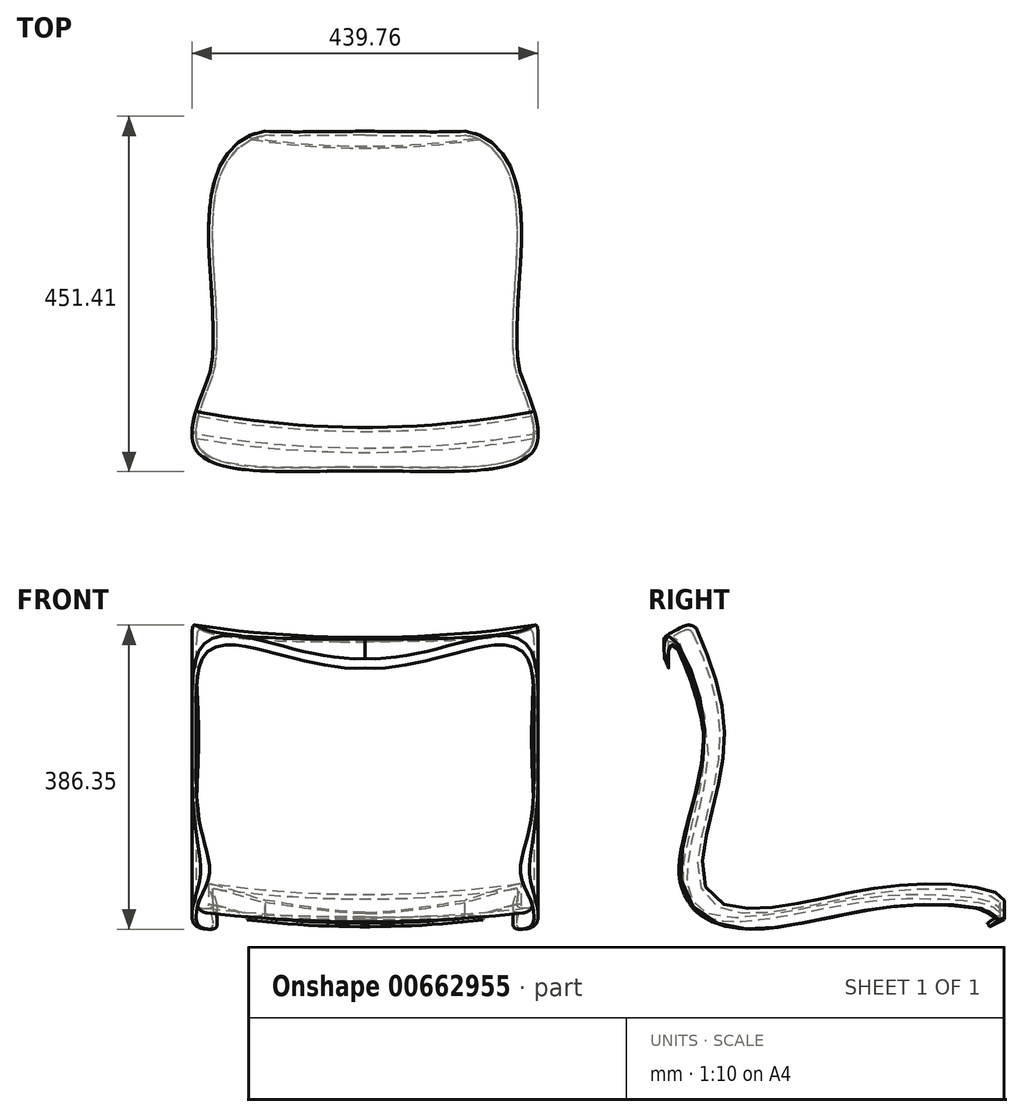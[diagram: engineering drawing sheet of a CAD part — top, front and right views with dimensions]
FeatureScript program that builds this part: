
annotation { "Feature Type Name" : "Feature", "Feature Type Description" : "" }
export const myFeature = defineFeature(function(context is Context, id is Id, definition is map)
    precondition{}
    {
        {
            var Q0;
            Q0=qCreatedBy(makeId("Right.planeOp"),FACE);
            var sketch = newSketch(context, id + "F0", { "sketchPlane" : qUnion([Q0])});
            skFitSpline(sketch, "E0", {"points": [v(-203.66, 209.62) * mm, v(-162.36, 57.64) * mm, v(-188.8, -91.05) * mm, v(-162.36, -145.98) * mm, v(12.76, -129.04) * mm, v(138.3, -122.44) * mm, v(204.4, -134) * mm, v(217.6, -150.52) * mm], "startDerivative": vector(355.5, -818.25) * mm, "endDerivative": vector(135.77, -275.04) * mm});
            skLineSegment(sketch, "E1", {"start": v(473.06, 770.55) * mm, "end": v(854.91, 242.64) * mm, "construction": true});
            skFitSpline(sketch, "E2.0", {"points": [v(-226.96, 199.5) * mm, v(-223.26, 191) * mm, v(-215.95, 174.12) * mm, v(-207.6, 153.32) * mm, v(-201.72, 136.84) * mm, v(-197.79, 124.55) * mm, v(-194.4, 112.35) * mm, v(-191.62, 100.21) * mm, v(-189.51, 88.14) * mm, v(-188.38, 78.11) * mm, v(-187.86, 70.1) * mm, v(-187.72, 65.1) * mm, v(-187.7, 61.1) * mm, v(-187.75, 58.09) * mm, v(-187.85, 55.06) * mm, v(-188.05, 50.99) * mm, v(-188.44, 45.82) * mm, v(-189.33, 37.4) * mm, v(-190.89, 26.65) * mm, v(-193.35, 13.47) * mm, v(-196.24, 0.13) * mm, v(-199.42, -13.31) * mm, v(-202.7, -26.76) * mm, v(-205.94, -40.17) * mm, v(-208.93, -53.5) * mm, v(-211.07, -64.52) * mm, v(-212.47, -73.3) * mm, v(-213.33, -79.87) * mm, v(-213.98, -86.42) * mm, v(-214.36, -92.98) * mm, v(-214.45, -99.5) * mm, v(-214.14, -108.15) * mm, v(-213.1, -116.75) * mm, v(-211.11, -125.26) * mm, v(-209.09, -131.58) * mm, v(-206.46, -137.79) * mm, v(-203.17, -143.82) * mm, v(-199.19, -149.56) * mm, v(-194.5, -154.92) * mm, v(-189.16, -159.75) * mm, v(-184.21, -163.27) * mm, v(-180.02, -165.74) * mm, v(-176.76, -167.43) * mm, v(-173.4, -168.94) * mm, v(-169.96, -170.29) * mm, v(-166.48, -171.44) * mm, v(-161.82, -172.77) * mm, v(-155.94, -174.06) * mm, v(-148.8, -175.11) * mm, v(-139.13, -175.98) * mm, v(-126.76, -176.2) * mm, v(-111.4, -175.4) * mm, v(-95.57, -173.78) * mm, v(-79.36, -171.54) * mm, v(-62.91, -168.84) * mm, v(-46.38, -165.85) * mm, v(-29.96, -162.72) * mm, v(-16.53, -160.13) * mm, v(-6.05, -158.15) * mm, v(1.66, -156.73) * mm, v(7.93, -155.61) * mm, v(12.84, -154.77) * mm, v(16.45, -154.17) * mm, v(20.02, -153.6) * mm, v(24.7, -152.88) * mm, v(30.45, -152.04) * mm, v(37.17, -151.14) * mm, v(45.9, -150.07) * mm, v(56.43, -148.98) * mm, v(68.52, -148) * mm, v(80.14, -147.35) * mm, v(91.37, -146.98) * mm, v(102.29, -146.85) * mm, v(112.98, -146.94) * mm, v(121.76, -147.16) * mm, v(128.75, -147.42) * mm, v(133.12, -147.61) * mm, v(136.6, -147.78) * mm, v(140.1, -147.96) * mm, v(144.41, -148.2) * mm, v(149.5, -148.52) * mm, v(156.12, -149) * mm, v(164.02, -149.73) * mm, v(171.22, -150.64) * mm, v(176.41, -151.48) * mm, v(179.98, -152.16) * mm, v(183.17, -152.88) * mm, v(185.93, -153.63) * mm, v(187.83, -154.25) * mm, v(189.06, -154.7) * mm, v(189.84, -155.03) * mm, v(190.47, -155.31) * mm, v(190.85, -155.5) * mm, v(191.07, -155.63) * mm, v(191.2, -155.7) * mm, v(191.27, -155.75) * mm, v(191.37, -155.81) * mm, v(191.44, -155.87) * mm, v(191.52, -155.93) * mm, v(191.58, -155.98) * mm, v(191.72, -156.13) * mm, v(192, -156.5) * mm, v(192.45, -157.18) * mm, v(193.06, -158.25) * mm, v(193.84, -159.75) * mm, v(194.48, -161.05) * mm, v(194.83, -161.76) * mm]});
            skLineSegment(sketch, "E3", {"start": v(-203.66, 209.62) * mm, "end": v(-226.96, 199.5) * mm});
            skLineSegment(sketch, "E4", {"start": v(194.83, -161.76) * mm, "end": v(217.6, -150.52) * mm});
            skSolve(sketch);
        }
        {
            var Q0;
            Q0 = qSketchRegion(id + "F0", true);
            var Q1;
            Q1 = qConstructionFilter(qBodyType(qCreatedBy(id + "F0" ,EDGE), BodyType.WIRE), ConstructionObject.NO);
            var Q2;
            Q2=sQuery(id+"F0.wireOp",EDGE,"E1");
            revolve(context, id + "F1", {"entities" : qUnion([Q0]), "surfaceEntities" : qUnion([Q1]), "axis" : qUnion([Q2]), "revolveType" : RevolveType.SYMMETRIC, "angle" : 35 * degree});
        }
        {
            var Q0;
            Q0=qCreatedBy(makeId("Top.planeOp"),FACE);
            var sketch = newSketch(context, id + "F2", { "sketchPlane" : qUnion([Q0])});
            skFitSpline(sketch, "E5", {"points": [v(-126.8, 213.83) * mm, v(-188.06, 160.83) * mm, v(-194.5, 0) * mm, v(-194.48, -78.42) * mm, v(-203.2, -108.9) * mm, v(-213.32, -192.95) * mm, v(0, -217.97) * mm], "startDerivative": vector(-512.5, -48.9) * mm, "endDerivative": vector(946.38, -22.1) * mm});
            skFitSpline(sketch, "E6", {"points": [v(-126.8, 213.83) * mm, v(0, 213.83) * mm], "startDerivative": vector(116.19, -4.65) * mm, "endDerivative": vector(116.45, 0) * mm});
            skLineSegment(sketch, "E7", {"start": v(0, 213.83) * mm, "end": v(0, -199.96) * mm, "construction": true});
            skFitSpline(sketch, "E8.MirrorCS", {"points": [v(126.8, 213.83) * mm, v(188.06, 160.83) * mm, v(194.5, 0) * mm, v(194.48, -78.42) * mm, v(203.2, -108.9) * mm, v(213.32, -192.95) * mm, v(0, -217.97) * mm], "startDerivative": vector(512.5, -48.9) * mm, "endDerivative": vector(-946.38, -22.1) * mm});
            skFitSpline(sketch, "E9.MirrorCS", {"points": [v(126.8, 213.83) * mm, v(0, 213.83) * mm], "startDerivative": vector(-116.19, -4.65) * mm, "endDerivative": vector(-116.45, 0) * mm});
            skSolve(sketch);
        }
        {
            var Q0;
            Q0=makeQuery(id+"F2.imprint","IMPRINT",FACE,{"disambiguationData":[TD([[makeQuery(id+"F2.imprint","IMPRINT",EDGE,{"derivedFrom":sQuery(id+"F2.wireOp",EDGE,"E5")}),1.0]])]});
            extrude(context, id + "F3", {"entities" : qUnion([Q0]), "operationType" : NewBodyOperationType.INTERSECT, "endBound" : BoundingType.SYMMETRIC, "oppositeDirection" : true, "depth" : 1016 * mm, "offsetDistance" : 25.4 * mm});
        }
        {
            var Q0;
            Q0=makeQuery(id+"F1.opRevolve","SWEPT_EDGE",EDGE,{"disambiguationData":[OSD([sQuery(id+"F0.wireOp",EDGE,"E0"),sQuery(id+"F0.wireOp",EDGE,"E3")])]});
            var Q1;
            Q1=makeQuery(id+"F3.boolean.opBoolean","INTERSECT",EDGE,{"derivedFrom":[makeQuery(id+"F1.opRevolve","SWEPT_FACE",FACE,{"disambiguationData":[OSD([sQuery(id+"F0.wireOp",EDGE,"E0")])]}),makeQuery(id+"F3.boolean.toolComplement.opBoolean","COPY",FACE,{"derivedFrom":makeQuery(id+"F3.opExtrude","SWEPT_FACE",FACE,{"disambiguationData":[OSD([sQuery(id+"F2.wireOp",EDGE,"E5")])]})})]});
            var Q2;
            Q2=makeQuery(id+"F3.boolean.opBoolean","INTERSECT",EDGE,{"derivedFrom":[makeQuery(id+"F1.opRevolve","SWEPT_FACE",FACE,{"disambiguationData":[OSD([sQuery(id+"F0.wireOp",EDGE,"E0")])]}),makeQuery(id+"F3.boolean.toolComplement.opBoolean","COPY",FACE,{"derivedFrom":makeQuery(id+"F3.opExtrude","SWEPT_FACE",FACE,{"disambiguationData":[OSD([sQuery(id+"F2.wireOp",EDGE,"E9.MirrorCS")])]})})]});
            var Q3;
            Q3=makeQuery(id+"F3.boolean.opBoolean","INTERSECT",EDGE,{"derivedFrom":[makeQuery(id+"F1.opRevolve","SWEPT_FACE",FACE,{"disambiguationData":[OSD([sQuery(id+"F0.wireOp",EDGE,"E0")])]}),makeQuery(id+"F3.boolean.toolComplement.opBoolean","COPY",FACE,{"derivedFrom":makeQuery(id+"F3.opExtrude","SWEPT_FACE",FACE,{"disambiguationData":[OSD([sQuery(id+"F2.wireOp",EDGE,"E6")])]})})]});
            var Q4;
            Q4=makeQuery(id+"F3.boolean.opBoolean","INTERSECT",EDGE,{"derivedFrom":[makeQuery(id+"F1.opRevolve","SWEPT_FACE",FACE,{"disambiguationData":[OSD([sQuery(id+"F0.wireOp",EDGE,"E0")])]}),makeQuery(id+"F3.boolean.toolComplement.opBoolean","COPY",FACE,{"derivedFrom":makeQuery(id+"F3.opExtrude","SWEPT_FACE",FACE,{"disambiguationData":[OSD([sQuery(id+"F2.wireOp",EDGE,"E8.MirrorCS")])]})})]});
            fillet(context, id + "F4", {"entities" : qUnion([Q0, Q1, Q2, Q3, Q4]), "radius" : 12.7 * mm, "tangentPropagation" : true, "allowEdgeOverflow" : false});
        }
        {
            var Q0;
            Q0=makeQuery(id+"F1.opRevolve","SWEPT_FACE",FACE,{"disambiguationData":[OSD([sQuery(id+"F0.wireOp",EDGE,"E2.0")])]});
            shell(context, id + "F5", {"entities" : qUnion([Q0]), "thickness" : 5.08 * mm});
        }
    });
